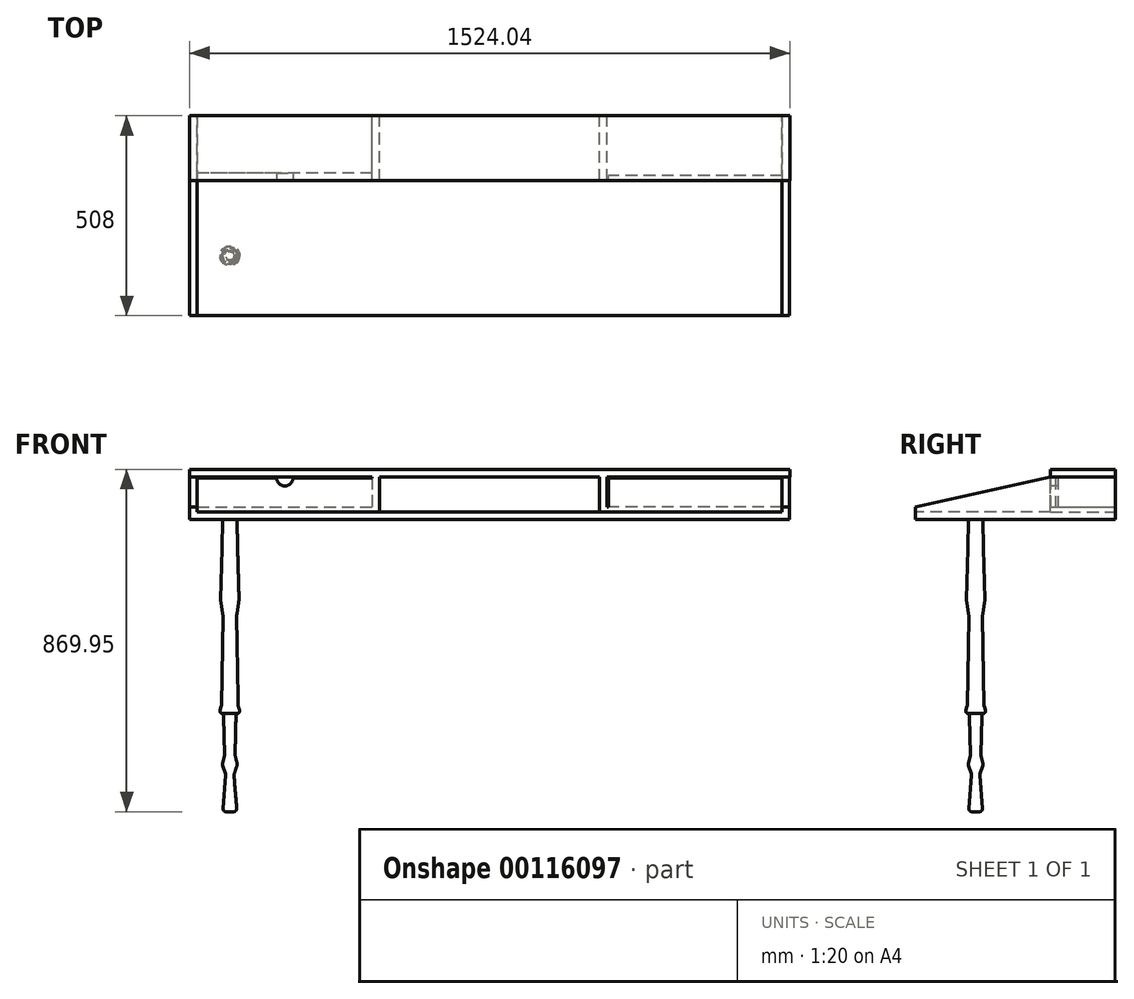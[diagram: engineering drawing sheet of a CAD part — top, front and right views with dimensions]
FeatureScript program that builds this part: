
annotation { "Feature Type Name" : "Feature", "Feature Type Description" : "" }
export const myFeature = defineFeature(function(context is Context, id is Id, definition is map)
    precondition{}
    {
        {
            var Q0;
            Q0=qCreatedBy(makeId("Top.planeOp"),FACE);
            var sketch = newSketch(context, id + "F0", { "sketchPlane" : qUnion([Q0])});
            skLineSegment(sketch, "E0.bottom", {"start": v(-6.35, 0) * mm, "end": v(1517.65, 0) * mm});
            skLineSegment(sketch, "E0.top", {"start": v(-6.35, -508) * mm, "end": v(1517.65, -508) * mm});
            skLineSegment(sketch, "E0.left", {"start": v(-6.35, 0) * mm, "end": v(-6.35, -508) * mm});
            skLineSegment(sketch, "E0.right", {"start": v(1517.65, 0) * mm, "end": v(1517.65, -508) * mm});
            skLineSegment(sketch, "E1", {"start": v(0, 0) * mm, "end": v(0, -508) * mm, "construction": true});
            skLineSegment(sketch, "E2", {"start": v(-6.35, -6.35) * mm, "end": v(1517.65, -6.35) * mm, "construction": true});
            skLineSegment(sketch, "E3", {"start": v(1511.3, 0) * mm, "end": v(1511.3, -508) * mm, "construction": true});
            skSolve(sketch);
        }
        {
            var Q0;
            Q0=makeQuery(id+"F0.imprint","IMPRINT",FACE,{"disambiguationData":[TD([[makeQuery(id+"F0.imprint","IMPRINT",EDGE,{"derivedFrom":sQuery(id+"F0.wireOp",EDGE,"E0.bottom")}),-1.0]])]});
            extrude(context, id + "F1", {"entities" : qUnion([Q0]), "depth" : 19.05 * mm});
        }
        {
            var Q0;
            Q0=makeQuery(id+"F1.opExtrude","SWEPT_FACE",FACE,{"disambiguationData":[OSD([sQuery(id+"F0.wireOp",EDGE,"E0.left")])]});
            var sketch = newSketch(context, id + "F2", { "sketchPlane" : qUnion([Q0])});
            skLineSegment(sketch, "E4", {"start": v(0, 19.05) * mm, "end": v(0, 107.95) * mm});
            skLineSegment(sketch, "E5", {"start": v(0, 107.95) * mm, "end": v(165.1, 107.95) * mm});
            skLineSegment(sketch, "E6", {"start": v(165.1, 107.95) * mm, "end": v(508, 31.75) * mm});
            skLineSegment(sketch, "E7", {"start": v(508, 31.75) * mm, "end": v(508, 19.05) * mm});
            skLineSegment(sketch, "E8", {"start": v(508, 19.05) * mm, "end": v(0, 19.05) * mm});
            skLineSegment(sketch, "E9", {"start": v(165.1, 107.95) * mm, "end": v(165.1, 19.05) * mm, "construction": true});
            skSolve(sketch);
        }
        {
            var Q0;
            Q0=makeQuery(id+"F2.imprint","IMPRINT",FACE,{"disambiguationData":[TD([[makeQuery(id+"F2.imprint","IMPRINT",EDGE,{"derivedFrom":sQuery(id+"F2.wireOp",EDGE,"E4")}),-1.0]])]});
            extrude(context, id + "F3", {"entities" : qUnion([Q0]), "oppositeDirection" : true, "depth" : 19.05 * mm});
        }
        {
            var Q0;
            Q0=qCreatedBy(makeId("Right.planeOp"),FACE);
            cPlane(context, id + "F4", {"entities" : qUnion([Q0]), "cplaneType" : CPlaneType.OFFSET, "offset" : 755.65 * mm, "width" : 152.4 * mm, "height" : 152.4 * mm});
        }
        {
            var Q0;
            Q0=makeQuery(id+"F3.opExtrude","SWEPT_BODY",BODY,{"disambiguationData":[OSD([sQuery(id+"F2.wireOp",EDGE,"E4"),sQuery(id+"F2.wireOp",EDGE,"E5"),sQuery(id+"F2.wireOp",EDGE,"E6"),sQuery(id+"F2.wireOp",EDGE,"E7"),sQuery(id+"F2.wireOp",EDGE,"E8")])]});
            var Q1;
            Q1=qCreatedBy(id+"F4.planeOp",FACE);
            mirror(context, id + "F5", {"operationType" : NewBodyOperationType.ADD, "entities" : qUnion([Q0]), "mirrorPlane" : qUnion([Q1])});
        }
        {
            var Q0;
            Q0=makeQuery(id+"F3.opExtrude","SWEPT_FACE",FACE,{"disambiguationData":[OSD([sQuery(id+"F2.wireOp",EDGE,"E5")])]});
            var sketch = newSketch(context, id + "F6", { "sketchPlane" : qUnion([Q0])});
            skLineSegment(sketch, "E10.bottom", {"start": v(-6.35, 0) * mm, "end": v(1517.7, 0) * mm});
            skLineSegment(sketch, "E10.top", {"start": v(-6.35, -165.1) * mm, "end": v(1517.7, -165.1) * mm});
            skLineSegment(sketch, "E10.left", {"start": v(-6.35, 0) * mm, "end": v(-6.35, -165.1) * mm});
            skLineSegment(sketch, "E10.right", {"start": v(1517.7, 0) * mm, "end": v(1517.7, -165.1) * mm});
            skPoint(sketch, "E11", {"position": v(-6.35, -165.1) * mm});
            skSolve(sketch);
        }
        {
            var Q0;
            Q0 = qSketchRegion(id + "F6", true);
            extrude(context, id + "F7", {"entities" : qUnion([Q0]), "operationType" : NewBodyOperationType.ADD, "depth" : 19.05 * mm});
        }
        {
            var Q0;
            Q0=qCreatedBy(makeId("Front.planeOp"),FACE);
            cPlane(context, id + "F8", {"entities" : qUnion([Q0]), "cplaneType" : CPlaneType.OFFSET, "offset" : 355.6 * mm, "width" : 152.4 * mm, "height" : 152.4 * mm});
        }
        {
            var Q0;
            Q0=qCreatedBy(id+"F8.planeOp",FACE);
            var sketch = newSketch(context, id + "F9", { "sketchPlane" : qUnion([Q0])});
            skLineSegment(sketch, "E12", {"start": v(95.25, 0) * mm, "end": v(95.25, -742.95) * mm});
            skLineSegment(sketch, "E13", {"start": v(76.87, 0) * mm, "end": v(75.48, -74.31) * mm});
            skLineSegment(sketch, "E14", {"start": v(75.47, -74.38) * mm, "end": v(71.85, -203.7) * mm});
            skLineSegment(sketch, "E15", {"start": v(71.92, -205.02) * mm, "end": v(78.01, -246.4) * mm});
            skLineSegment(sketch, "E16", {"start": v(78.1, -247.65) * mm, "end": v(73.85, -473.38) * mm});
            skLineSegment(sketch, "E17", {"start": v(73.46, -475.64) * mm, "end": v(70.51, -484.46) * mm});
            skLineSegment(sketch, "E18", {"start": v(74.34, -493.77) * mm, "end": v(75.33, -494.1) * mm});
            skLineSegment(sketch, "E19", {"start": v(79.54, -500.83) * mm, "end": v(81.76, -598.6) * mm});
            skLineSegment(sketch, "E20", {"start": v(81.54, -600.6) * mm, "end": v(76.5, -620.92) * mm});
            skLineSegment(sketch, "E21", {"start": v(76.7, -625.22) * mm, "end": v(84.3, -647.47) * mm});
            skLineSegment(sketch, "E22", {"start": v(84.7, -650.56) * mm, "end": v(77.72, -734.7) * mm});
            skLineSegment(sketch, "E23", {"start": v(85.31, -742.95) * mm, "end": v(95.25, -742.95) * mm});
            skLineSegment(sketch, "E24", {"start": v(76.87, 0) * mm, "end": v(95.25, 0) * mm});
            skPoint(sketch, "E25.visualSharp", {"position": v(71.83, -204.36) * mm});
            skArc(sketch, "E25.filletArc", {"start": v(71.85, -203.7) * mm, "mid": v(71.86, -204.36) * mm, "end": v(71.92, -205.02) * mm});
            skPoint(sketch, "E26.visualSharp", {"position": v(75.47, -74.35) * mm});
            skArc(sketch, "E26.filletArc", {"start": v(75.47, -74.38) * mm, "mid": v(75.47, -74.35) * mm, "end": v(75.48, -74.31) * mm});
            skPoint(sketch, "E27.visualSharp", {"position": v(78.1, -247.02) * mm});
            skArc(sketch, "E27.filletArc", {"start": v(78.1, -247.65) * mm, "mid": v(78.08, -247.02) * mm, "end": v(78.01, -246.4) * mm});
            skPoint(sketch, "E28.visualSharp", {"position": v(73.82, -474.54) * mm});
            skArc(sketch, "E28.filletArc", {"start": v(73.46, -475.64) * mm, "mid": v(73.74, -474.53) * mm, "end": v(73.85, -473.38) * mm});
            skPoint(sketch, "E29.visualSharp", {"position": v(68.1, -491.7) * mm});
            skArc(sketch, "E29.filletArc", {"start": v(70.51, -484.46) * mm, "mid": v(70.93, -490.28) * mm, "end": v(75.33, -494.1) * mm});
            skPoint(sketch, "E30.visualSharp", {"position": v(79.42, -495.47) * mm});
            skArc(sketch, "E30.filletArc", {"start": v(79.54, -500.83) * mm, "mid": v(78.06, -496.48) * mm, "end": v(74.34, -493.77) * mm});
            skPoint(sketch, "E31.visualSharp", {"position": v(75.97, -623.1) * mm});
            skArc(sketch, "E31.filletArc", {"start": v(76.5, -620.92) * mm, "mid": v(76.3, -623.08) * mm, "end": v(76.7, -625.22) * mm});
            skPoint(sketch, "E32.visualSharp", {"position": v(84.82, -648.97) * mm});
            skArc(sketch, "E32.filletArc", {"start": v(84.7, -650.56) * mm, "mid": v(84.66, -649) * mm, "end": v(84.3, -647.47) * mm});
            skPoint(sketch, "E33.visualSharp", {"position": v(77.03, -742.95) * mm});
            skArc(sketch, "E33.filletArc", {"start": v(77.72, -734.7) * mm, "mid": v(79.7, -740.5) * mm, "end": v(85.31, -742.95) * mm});
            skPoint(sketch, "E34.visualSharp", {"position": v(81.79, -599.62) * mm});
            skArc(sketch, "E34.filletArc", {"start": v(81.54, -600.6) * mm, "mid": v(81.72, -599.61) * mm, "end": v(81.76, -598.6) * mm});
            skSolve(sketch);
        }
        {
            var Q0;
            Q0 = qSketchRegion(id + "F9", true);
            var Q1;
            Q1=sQuery(id+"F9.wireOp",EDGE,"E12");
            revolve(context, id + "F10", {"operationType" : NewBodyOperationType.ADD, "entities" : qUnion([Q0]), "axis" : qUnion([Q1]), "revolveType" : RevolveType.FULL});
        }
        {
            var Q0;
            {var subQ0=makeQuery(id+"F3.opExtrude","SWEPT_FACE",FACE,{"disambiguationData":[OSD([sQuery(id+"F2.wireOp",EDGE,"E4")])]});Q0=makeQuery(id+"F7.boolean.opBoolean","MERGE",FACE,{"derivedFrom":[makeQuery(id+"F5.boolean.opBoolean","MERGE",FACE,{"derivedFrom":[makeQuery(id+"F1.opExtrude","SWEPT_FACE",FACE,{"disambiguationData":[OSD([sQuery(id+"F0.wireOp",EDGE,"E0.bottom")])]}),subQ0,makeQuery(id+"F5.opPattern","COPY",FACE,{"derivedFrom":subQ0,"instanceName":"1"})]}),makeQuery(id+"F7.opExtrude","SWEPT_FACE",FACE,{"disambiguationData":[OSD([sQuery(id+"F6.wireOp",EDGE,"E10.bottom")])]})]});}
            var sketch = newSketch(context, id + "F11", { "sketchPlane" : qUnion([Q0])});
            skLineSegment(sketch, "E35.bottom", {"start": v(-476.27, 107.95) * mm, "end": v(-457.22, 107.95) * mm});
            skLineSegment(sketch, "E35.top", {"start": v(-476.27, 19.05) * mm, "end": v(-457.22, 19.05) * mm});
            skLineSegment(sketch, "E35.left", {"start": v(-476.27, 107.95) * mm, "end": v(-476.27, 19.05) * mm});
            skLineSegment(sketch, "E35.right", {"start": v(-457.22, 107.95) * mm, "end": v(-457.22, 19.05) * mm});
            skLineSegment(sketch, "E36.bottom", {"start": v(-1054.12, 107.95) * mm, "end": v(-1035.07, 107.95) * mm});
            skLineSegment(sketch, "E36.top", {"start": v(-1054.12, 19.05) * mm, "end": v(-1035.07, 19.05) * mm});
            skLineSegment(sketch, "E36.left", {"start": v(-1054.12, 107.95) * mm, "end": v(-1054.12, 19.05) * mm});
            skLineSegment(sketch, "E36.right", {"start": v(-1035.07, 107.95) * mm, "end": v(-1035.07, 19.05) * mm});
            skLineSegment(sketch, "E37", {"start": v(-755.67, 107.95) * mm, "end": v(-755.67, 19.05) * mm, "construction": true});
            skPoint(sketch, "E37.startSnap0", {"position": v(-755.67, 127) * mm});
            skLineSegment(sketch, "E38", {"start": v(-476.27, 63.5) * mm, "end": v(-1035.07, 63.5) * mm, "construction": true});
            skPoint(sketch, "E39", {"position": v(-755.67, 63.5) * mm});
            skSolve(sketch);
        }
        {
            var Q0;
            Q0 = qSketchRegion(id + "F11", true);
            var Q1;
            Q1=makeQuery(id+"F7.opExtrude","SWEPT_FACE",FACE,{"disambiguationData":[OSD([sQuery(id+"F6.wireOp",EDGE,"E10.top")])]});
            extrude(context, id + "F12", {"entities" : qUnion([Q0]), "operationType" : NewBodyOperationType.ADD, "endBound" : BoundingType.UP_TO_SURFACE, "oppositeDirection" : true, "endBoundEntityFace" : qUnion([Q1]), "depth" : 25.4 * mm});
        }
        {
            var Q0;
            Q0=makeQuery(id+"F7.boolean.opBoolean","MERGE",FACE,{"derivedFrom":[makeQuery(id+"F5.boolean.opBoolean","MERGE",FACE,{"derivedFrom":[makeQuery(id+"F1.opExtrude","SWEPT_FACE",FACE,{"disambiguationData":[OSD([sQuery(id+"F0.wireOp",EDGE,"E0.left")])]}),makeQuery(id+"F3.opExtrude","CAP_FACE",FACE,{"disambiguationData":[OSD([sQuery(id+"F2.wireOp",EDGE,"E4"),sQuery(id+"F2.wireOp",EDGE,"E5"),sQuery(id+"F2.wireOp",EDGE,"E6"),sQuery(id+"F2.wireOp",EDGE,"E7"),sQuery(id+"F2.wireOp",EDGE,"E8")])],"isStart":true})]}),makeQuery(id+"F7.opExtrude","SWEPT_FACE",FACE,{"disambiguationData":[OSD([sQuery(id+"F6.wireOp",EDGE,"E10.left")])]})]});
            var sketch = newSketch(context, id + "F13", { "sketchPlane" : qUnion([Q0])});
            skLineSegment(sketch, "E40.bottom", {"start": v(203.2, 146.05) * mm, "end": v(508, 146.05) * mm});
            skLineSegment(sketch, "E40.top", {"start": v(203.2, 18.55) * mm, "end": v(508, 18.55) * mm});
            skLineSegment(sketch, "E40.left", {"start": v(203.2, 146.05) * mm, "end": v(203.2, 18.55) * mm});
            skLineSegment(sketch, "E40.right", {"start": v(508, 146.05) * mm, "end": v(508, 18.55) * mm});
            skSolve(sketch);
        }
        {
            var Q0;
            {var subQ0=makeQuery(id+"F3.opExtrude","SWEPT_FACE",FACE,{"disambiguationData":[OSD([sQuery(id+"F2.wireOp",EDGE,"E4")])]});Q0=makeQuery(id+"F12.boolean.opBoolean","MERGE",FACE,{"derivedFrom":[makeQuery(id+"F7.boolean.opBoolean","MERGE",FACE,{"derivedFrom":[makeQuery(id+"F5.boolean.opBoolean","MERGE",FACE,{"derivedFrom":[makeQuery(id+"F1.opExtrude","SWEPT_FACE",FACE,{"disambiguationData":[OSD([sQuery(id+"F0.wireOp",EDGE,"E0.bottom")])]}),subQ0,makeQuery(id+"F5.opPattern","COPY",FACE,{"derivedFrom":subQ0,"instanceName":"1"})]}),makeQuery(id+"F7.opExtrude","SWEPT_FACE",FACE,{"disambiguationData":[OSD([sQuery(id+"F6.wireOp",EDGE,"E10.bottom")])]})]}),makeQuery(id+"F12.opExtrude","CAP_FACE",FACE,{"disambiguationData":[OSD([sQuery(id+"F11.wireOp",EDGE,"E35.bottom"),sQuery(id+"F11.wireOp",EDGE,"E35.top"),sQuery(id+"F11.wireOp",EDGE,"E35.left"),sQuery(id+"F11.wireOp",EDGE,"E35.right")])],"isStart":true}),makeQuery(id+"F12.opExtrude","CAP_FACE",FACE,{"disambiguationData":[OSD([sQuery(id+"F11.wireOp",EDGE,"E36.bottom"),sQuery(id+"F11.wireOp",EDGE,"E36.top"),sQuery(id+"F11.wireOp",EDGE,"E36.left"),sQuery(id+"F11.wireOp",EDGE,"E36.right")])],"isStart":true})]});}
            var sketch = newSketch(context, id + "F14", { "sketchPlane" : qUnion([Q0])});
            skLineSegment(sketch, "E41.bottom", {"start": v(-12.7, 31.75) * mm, "end": v(-457.22, 31.75) * mm});
            skLineSegment(sketch, "E41.top", {"start": v(-12.7, 19.05) * mm, "end": v(-457.22, 19.05) * mm});
            skLineSegment(sketch, "E41.left", {"start": v(-12.7, 31.75) * mm, "end": v(-12.7, 19.05) * mm});
            skLineSegment(sketch, "E41.right", {"start": v(-457.22, 31.75) * mm, "end": v(-457.22, 19.05) * mm});
            skLineSegment(sketch, "E42.bottom", {"start": v(-1498.6, 31.75) * mm, "end": v(-1054.12, 31.75) * mm});
            skLineSegment(sketch, "E42.top", {"start": v(-1498.6, 19.05) * mm, "end": v(-1054.12, 19.05) * mm});
            skLineSegment(sketch, "E42.left", {"start": v(-1498.6, 31.75) * mm, "end": v(-1498.6, 19.05) * mm});
            skLineSegment(sketch, "E42.right", {"start": v(-1054.12, 31.75) * mm, "end": v(-1054.12, 19.05) * mm});
            skSolve(sketch);
        }
        {
            var Q0;
            Q0 = qSketchRegion(id + "F14", true);
            extrude(context, id + "F15", {"entities" : qUnion([Q0]), "operationType" : NewBodyOperationType.ADD, "oppositeDirection" : true, "depth" : 165.1 * mm});
        }
        {
            var Q0;
            Q0=makeQuery(id+"F15.opExtrude","SWEPT_FACE",FACE,{"disambiguationData":[OSD([sQuery(id+"F14.wireOp",EDGE,"E41.bottom")])]});
            var sketch = newSketch(context, id + "F16", { "sketchPlane" : qUnion([Q0])});
            skLineSegment(sketch, "E43.bottom", {"start": v(457.22, -165.1) * mm, "end": v(12.7, -165.1) * mm});
            skLineSegment(sketch, "E43.top", {"start": v(457.22, -146.05) * mm, "end": v(12.7, -146.05) * mm});
            skLineSegment(sketch, "E43.left", {"start": v(457.22, -165.1) * mm, "end": v(457.22, -146.05) * mm});
            skLineSegment(sketch, "E43.right", {"start": v(12.7, -165.1) * mm, "end": v(12.7, -146.05) * mm});
            skLineSegment(sketch, "E44.bottom", {"start": v(1501.66, -165.1) * mm, "end": v(1057.14, -165.1) * mm});
            skLineSegment(sketch, "E44.top", {"start": v(1501.66, -152.4) * mm, "end": v(1057.14, -152.4) * mm});
            skLineSegment(sketch, "E44.left", {"start": v(1501.66, -165.1) * mm, "end": v(1501.66, -152.4) * mm});
            skLineSegment(sketch, "E44.right", {"start": v(1057.14, -165.1) * mm, "end": v(1057.14, -152.4) * mm});
            skSolve(sketch);
        }
        {
            var Q0;
            Q0 = qSketchRegion(id + "F16", true);
            extrude(context, id + "F17", {"entities" : qUnion([Q0]), "operationType" : NewBodyOperationType.ADD, "depth" : 73.66 * mm});
        }
        {
            var Q0;
            Q0=makeQuery(id+"F17.boolean.opBoolean","MERGE",FACE,{"derivedFrom":[makeQuery(id+"F15.opExtrude","CAP_FACE",FACE,{"disambiguationData":[OSD([sQuery(id+"F14.wireOp",EDGE,"E41.bottom"),sQuery(id+"F14.wireOp",EDGE,"E41.top"),sQuery(id+"F14.wireOp",EDGE,"E41.left"),sQuery(id+"F14.wireOp",EDGE,"E41.right")])],"isStart":false}),makeQuery(id+"F17.opExtrude","SWEPT_FACE",FACE,{"disambiguationData":[OSD([sQuery(id+"F16.wireOp",EDGE,"E43.bottom")])]})]});
            var sketch = newSketch(context, id + "F18", { "sketchPlane" : qUnion([Q0])});
            skLineSegment(sketch, "E45", {"start": v(12.7, 105.41) * mm, "end": v(457.22, 105.4) * mm, "construction": true});
            skPoint(sketch, "E46", {"position": v(234.96, 105.41) * mm});
            skArc(sketch, "E47", {"start": v(213.84, 105.41) * mm, "mid": v(234.96, 84.3) * mm, "end": v(256.08, 105.41) * mm});
            skSolve(sketch);
        }
        {
            var Q0;
            {var subQ0=sQuery(id+"F18.wireOp",EDGE,"E47");Q0=makeQuery(id+"F18.imprint","IMPRINT",FACE,{"disambiguationData":[TD([[makeQuery(id+"F18.imprint","IMPRINT",EDGE,{"derivedFrom":subQ0}),1.0]])]});}
            extrude(context, id + "F19", {"entities" : qUnion([Q0]), "operationType" : NewBodyOperationType.REMOVE, "endBound" : BoundingType.THROUGH_ALL, "oppositeDirection" : true, "depth" : 25.4 * mm});
        }
    });
